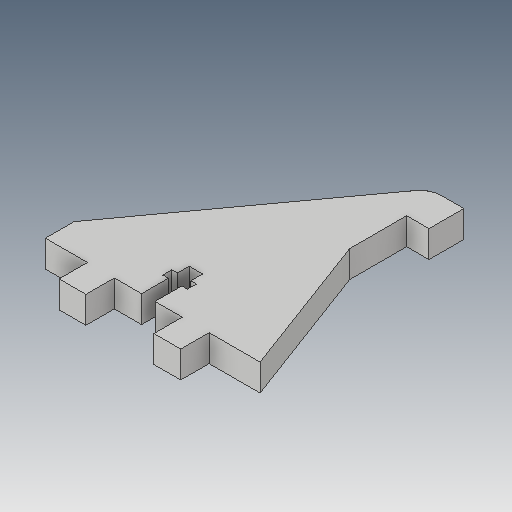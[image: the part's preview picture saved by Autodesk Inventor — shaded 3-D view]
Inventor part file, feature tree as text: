
AUTODESK INVENTOR PART (.ipt)
format: ipt  version: 2017 (Build 210142000, 142)  size: 120,320 bytes
history: native  units: mm
features: extrude x1, sketch x1
ambient origin geometry x8: Origin, YZ Plane, XZ Plane, XY Plane, X Axis, Y Axis, Z Axis, Center Point
bodies: Solid1 (feature_tree)
feature tree (2):
  extrude  "Extrusion1"  [1 undecoded]
  sketch  "Sketch1"  dims[d0=6.0mm d1=0.0mm]
note: 1 required parameter value undecoded (feature->parameter linkage not recoverable at this tier; creation-order binding heuristic only, values carry confidence <= 0.55)
